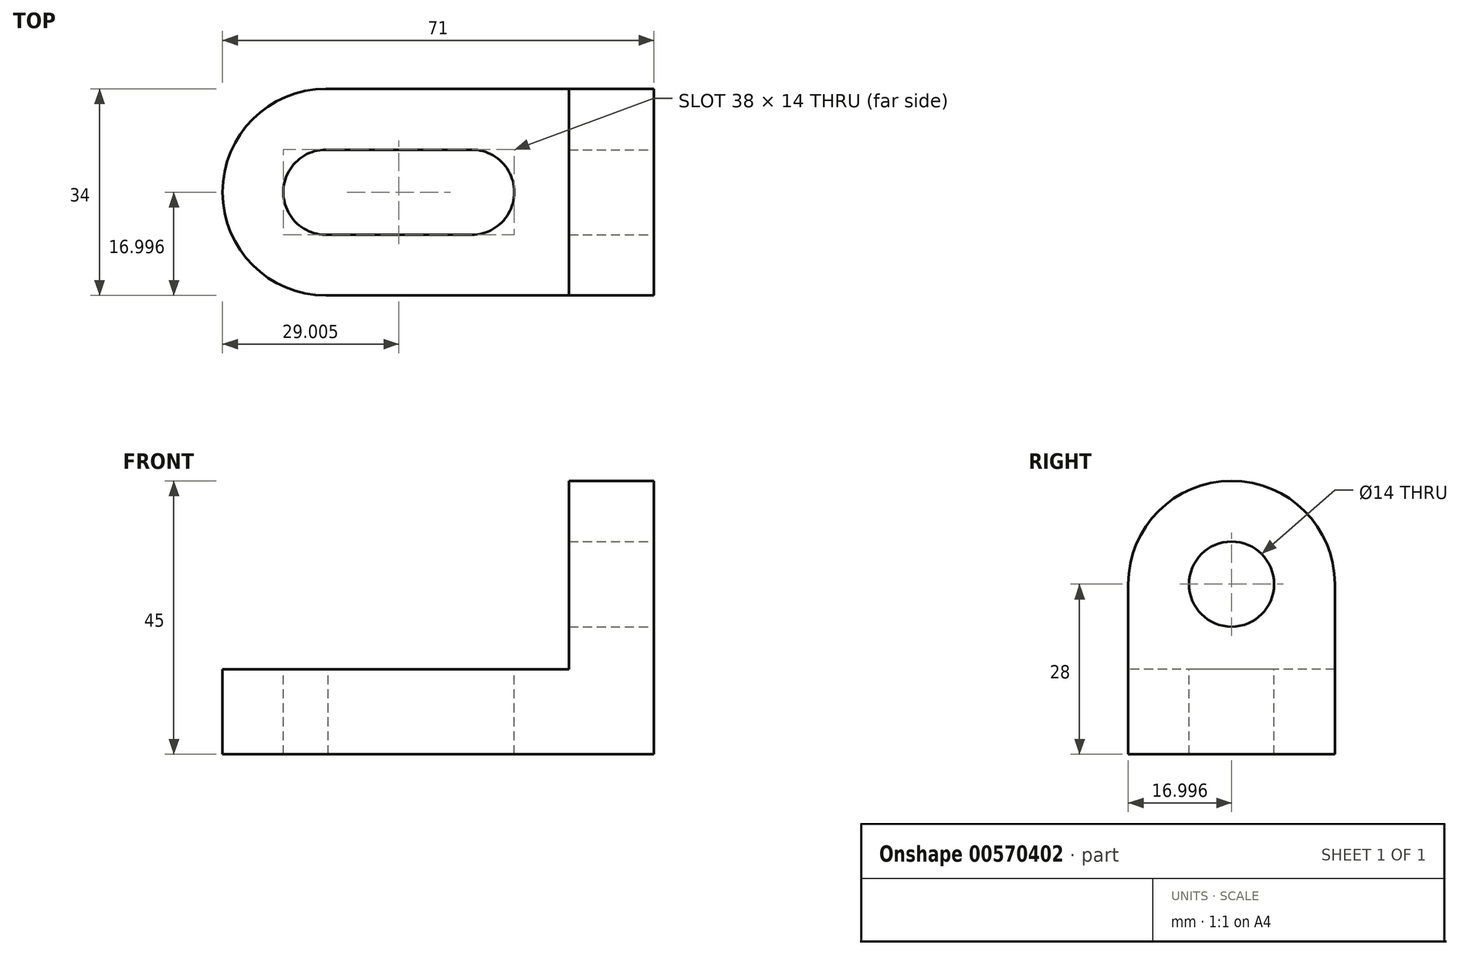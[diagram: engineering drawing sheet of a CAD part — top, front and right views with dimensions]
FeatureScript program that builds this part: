
annotation { "Feature Type Name" : "Feature", "Feature Type Description" : "" }
export const myFeature = defineFeature(function(context is Context, id is Id, definition is map)
    precondition{}
    {
        {
            var Q0;
            Q0=qCreatedBy(makeId("Top.planeOp"),FACE);
            var sketch = newSketch(context, id + "F0", { "sketchPlane" : qUnion([Q0])});
            skLineSegment(sketch, "E0.bottom", {"start": v(-28.27, -13.53) * mm, "end": v(25.73, -13.53) * mm});
            skLineSegment(sketch, "E0.top", {"start": v(-28.27, 20.47) * mm, "end": v(25.73, 20.47) * mm});
            skLineSegment(sketch, "E0.left", {"start": v(-28.27, -13.53) * mm, "end": v(-28.27, 20.47) * mm});
            skLineSegment(sketch, "E0.right", {"start": v(25.73, -13.53) * mm, "end": v(25.73, 20.47) * mm});
            skSolve(sketch);
        }
        {
            var Q0;
            Q0=makeQuery(id+"F0.imprint","IMPRINT",FACE,{"disambiguationData":[TD([[makeQuery(id+"F0.imprint","IMPRINT",EDGE,{"derivedFrom":sQuery(id+"F0.wireOp",EDGE,"E0.bottom")}),1.0]])]});
            extrude(context, id + "F1", {"entities" : qUnion([Q0]), "depth" : 14 * mm, "offsetDistance" : 25 * mm});
        }
        {
            var Q0;
            Q0=makeQuery(id+"F1.opExtrude","CAP_FACE",FACE,{"disambiguationData":[OSD([sQuery(id+"F0.wireOp",EDGE,"E0.bottom"),sQuery(id+"F0.wireOp",EDGE,"E0.top"),sQuery(id+"F0.wireOp",EDGE,"E0.left"),sQuery(id+"F0.wireOp",EDGE,"E0.right")])],"isStart":false});
            var sketch = newSketch(context, id + "F2", { "sketchPlane" : qUnion([Q0])});
            skLineSegment(sketch, "E1.bottom", {"start": v(25.73, 20.47) * mm, "end": v(11.73, 20.47) * mm});
            skLineSegment(sketch, "E1.top", {"start": v(25.73, -13.53) * mm, "end": v(11.73, -13.53) * mm});
            skLineSegment(sketch, "E1.left", {"start": v(25.73, 20.47) * mm, "end": v(25.73, -13.53) * mm});
            skLineSegment(sketch, "E1.right", {"start": v(11.73, 20.47) * mm, "end": v(11.73, -13.53) * mm});
            skSolve(sketch);
        }
        {
            var Q0;
            Q0=makeQuery(id+"F2.imprint","IMPRINT",FACE,{"disambiguationData":[TD([[makeQuery(id+"F2.imprint","IMPRINT",EDGE,{"derivedFrom":sQuery(id+"F2.wireOp",EDGE,"E1.bottom")}),-1.0]])]});
            extrude(context, id + "F3", {"entities" : qUnion([Q0]), "operationType" : NewBodyOperationType.ADD, "depth" : 14 * mm, "offsetDistance" : 25 * mm});
        }
        {
            var Q0;
            Q0=makeQuery(id+"F3.boolean.opBoolean","MERGE",FACE,{"derivedFrom":[makeQuery(id+"F1.opExtrude","SWEPT_FACE",FACE,{"disambiguationData":[OSD([sQuery(id+"F0.wireOp",EDGE,"E0.right")])]}),makeQuery(id+"F3.opExtrude","SWEPT_FACE",FACE,{"disambiguationData":[OSD([sQuery(id+"F2.wireOp",EDGE,"E1.left")])]})]});
            var sketch = newSketch(context, id + "F4", { "sketchPlane" : qUnion([Q0])});
            skCircle(sketch, "E2", {"center": v(3.47, 28) * mm, "radius": 17 * mm});
            skSolve(sketch);
        }
        {
            var Q0;
            {var subQ1=sQuery(id+"F2.wireOp",EDGE,"E1.left");var subQ3=makeQuery(id+"F3.opExtrude","CAP_EDGE",EDGE,{"disambiguationData":[OSD([subQ1])],"isStart":false});Q0=makeQuery(id+"F4.imprint","IMPRINT",FACE,{"disambiguationData":[TD([[makeQuery(id+"F4.imprint","IMPRINT",EDGE,{"derivedFrom":subQ3}),1.0]])]});}
            extrude(context, id + "F5", {"entities" : qUnion([Q0]), "operationType" : NewBodyOperationType.ADD, "oppositeDirection" : true, "depth" : 14 * mm, "offsetDistance" : 25 * mm});
        }
        {
            var Q0;
            Q0=makeQuery(id+"F1.opExtrude","CAP_FACE",FACE,{"disambiguationData":[OSD([sQuery(id+"F0.wireOp",EDGE,"E0.bottom"),sQuery(id+"F0.wireOp",EDGE,"E0.top"),sQuery(id+"F0.wireOp",EDGE,"E0.left"),sQuery(id+"F0.wireOp",EDGE,"E0.right")])],"isStart":false});
            var sketch = newSketch(context, id + "F6", { "sketchPlane" : qUnion([Q0])});
            skCircle(sketch, "E3", {"center": v(-28.27, 3.47) * mm, "radius": 17 * mm});
            skSolve(sketch);
        }
        {
            var Q0;
            {var subQ1=makeQuery(id+"F1.opExtrude","CAP_EDGE",EDGE,{"disambiguationData":[OSD([sQuery(id+"F0.wireOp",EDGE,"E0.left")])],"isStart":false});Q0=makeQuery(id+"F6.imprint","IMPRINT",FACE,{"disambiguationData":[TD([[makeQuery(id+"F6.imprint","IMPRINT",EDGE,{"derivedFrom":subQ1}),1.0]])]});}
            extrude(context, id + "F7", {"entities" : qUnion([Q0]), "operationType" : NewBodyOperationType.ADD, "oppositeDirection" : true, "depth" : 14 * mm, "offsetDistance" : 25 * mm});
        }
        {
            var Q0;
            {var subQ0=sQuery(id+"F2.wireOp",EDGE,"E1.left");Q0=makeQuery(id+"F5.boolean.opBoolean","MERGE",FACE,{"derivedFrom":[makeQuery(id+"F3.boolean.opBoolean","MERGE",FACE,{"derivedFrom":[makeQuery(id+"F1.opExtrude","SWEPT_FACE",FACE,{"disambiguationData":[OSD([sQuery(id+"F0.wireOp",EDGE,"E0.right")])]}),makeQuery(id+"F3.opExtrude","SWEPT_FACE",FACE,{"disambiguationData":[OSD([subQ0])]})]}),makeQuery(id+"F5.opExtrude","CAP_FACE",FACE,{"disambiguationData":[OSD([subQ0,sQuery(id+"F4.wireOp",EDGE,"E2")])],"isStart":true})]});}
            var sketch = newSketch(context, id + "F8", { "sketchPlane" : qUnion([Q0])});
            skCircle(sketch, "E4", {"center": v(3.47, 28) * mm, "radius": 7 * mm});
            skSolve(sketch);
        }
        {
            var Q0;
            Q0=makeQuery(id+"F8.imprint","IMPRINT",FACE,{"disambiguationData":[TD([[makeQuery(id+"F8.imprint","IMPRINT",EDGE,{"derivedFrom":sQuery(id+"F8.wireOp",EDGE,"E4")}),1.0]])]});
            extrude(context, id + "F9", {"entities" : qUnion([Q0]), "operationType" : NewBodyOperationType.REMOVE, "oppositeDirection" : true, "depth" : 25 * mm, "offsetDistance" : 25 * mm});
        }
        {
            var Q0;
            {var subQ0=sQuery(id+"F0.wireOp",EDGE,"E0.left");Q0=makeQuery(id+"F7.boolean.opBoolean","MERGE",FACE,{"derivedFrom":[makeQuery(id+"F1.opExtrude","CAP_FACE",FACE,{"disambiguationData":[OSD([sQuery(id+"F0.wireOp",EDGE,"E0.bottom"),sQuery(id+"F0.wireOp",EDGE,"E0.top"),subQ0,sQuery(id+"F0.wireOp",EDGE,"E0.right")])],"isStart":false}),makeQuery(id+"F7.opExtrude","CAP_FACE",FACE,{"disambiguationData":[OSD([subQ0,sQuery(id+"F6.wireOp",EDGE,"E3")])],"isStart":true})]});}
            var sketch = newSketch(context, id + "F10", { "sketchPlane" : qUnion([Q0])});
            skCircle(sketch, "E5", {"center": v(-28.27, 3.47) * mm, "radius": 7 * mm});
            skCircle(sketch, "E6", {"center": v(-4.27, 3.47) * mm, "radius": 7 * mm});
            skLineSegment(sketch, "E7", {"start": v(-27.91, -3.52) * mm, "end": v(-4.27, -3.53) * mm});
            skLineSegment(sketch, "E8", {"start": v(-28.27, 10.47) * mm, "end": v(-4.27, 10.47) * mm});
            skSolve(sketch);
        }
        {
            var Q0;
            {var subQ0=sQuery(id+"F10.wireOp",EDGE,"E5");var subQ1=makeQuery(id+"F10.imprint","INTERSECT",VERTEX,{"derivedFrom":[subQ0,sQuery(id+"F10.wireOp",EDGE,"E7")]});Q0=makeQuery(id+"F10.imprint","IMPRINT",FACE,{"disambiguationData":[TD([[makeQuery(id+"F10.imprint","IMPRINT",EDGE,{"disambiguationData":[TD([[subQ1,1.0]])],"derivedFrom":subQ0}),1.0]])]});}
            var Q1;
            {var subQ0=sQuery(id+"F10.wireOp",EDGE,"E7");Q1=makeQuery(id+"F10.imprint","IMPRINT",FACE,{"disambiguationData":[TD([[makeQuery(id+"F10.imprint","IMPRINT",EDGE,{"derivedFrom":subQ0}),1.0]])]});}
            var Q2;
            {var subQ0=sQuery(id+"F10.wireOp",EDGE,"E6");var subQ1=makeQuery(id+"F10.imprint","INTERSECT",VERTEX,{"derivedFrom":[subQ0,sQuery(id+"F10.wireOp",EDGE,"E7")]});Q2=makeQuery(id+"F10.imprint","IMPRINT",FACE,{"disambiguationData":[TD([[makeQuery(id+"F10.imprint","IMPRINT",EDGE,{"disambiguationData":[TD([[subQ1,1.0]])],"derivedFrom":subQ0}),1.0]])]});}
            extrude(context, id + "F11", {"entities" : qUnion([Q0, Q1, Q2]), "operationType" : NewBodyOperationType.REMOVE, "oppositeDirection" : true, "depth" : 25 * mm, "offsetDistance" : 25 * mm});
        }
    });
